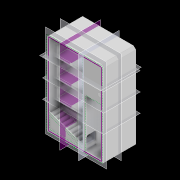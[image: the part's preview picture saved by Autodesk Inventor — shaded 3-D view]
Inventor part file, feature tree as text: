
AUTODESK INVENTOR PART (.ipt)
format: ipt  version: 2020 (Build 240168000, 168)  size: 2,139,136 bytes
history: native  units: mm
features: other x140, sketch x44, extrude x32, plane x15, mirror x15, pattern_linear x14, projected_geometry x8, chamfer x6, fillet x4, hole x2, loft x2
ambient origin geometry x8: Origin, YZ Plane, XZ Plane, XY Plane, X Axis, Y Axis, Z Axis, Center Point
bodies: Body1 (feature_tree), Body2 (feature_tree), Body3 (feature_tree), Body4 (feature_tree), Body5 (feature_tree), Body6 (feature_tree), Body7 (feature_tree), Body8 (feature_tree), Body9 (feature_tree), Body10 (feature_tree), Body11 (feature_tree), Body12 (feature_tree), Body13 (feature_tree), Body14 (feature_tree), Body15 (feature_tree), Body16 (feature_tree), Body17 (feature_tree), Body18 (feature_tree), Body19 (feature_tree), Body20 (feature_tree), Body21 (feature_tree), Body22 (feature_tree), Body23 (feature_tree), Body24 (feature_tree), Body25 (feature_tree), Body26 (feature_tree), Body27 (feature_tree), Body28 (feature_tree), Body29 (feature_tree), Body30 (feature_tree), Body31 (feature_tree), Body32 (feature_tree), Body33 (feature_tree), Body34 (feature_tree), Body35 (feature_tree), Body36 (feature_tree), Body37 (feature_tree), Body38 (feature_tree), Body39 (feature_tree), Body40 (feature_tree), Body41 (feature_tree), Body42 (feature_tree), Body43 (feature_tree), Body44 (feature_tree), Body45 (feature_tree), Body46 (feature_tree), Body47 (feature_tree), Body48 (feature_tree)
feature tree (282):
  other  "實體1"
  extrude  "擠出1"  Depth=1200.0mm
  plane  "工作平面1"
  plane  "工作平面2"
  other  "分割1"
  plane  "工作平面3"
  extrude  "擠出3"  Depth=800.0mm
  plane  "工作平面6"
  plane  "工作平面7"
  extrude  "擠出4"  Depth=1820.0mm TaperAngle=0.0deg
  hole  "孔1"  [1 undecoded]
  pattern_linear  "矩形陣列1"  Spacing1=-80.0mm  [1 undecoded]
  pattern_linear  "矩形陣列2"  Spacing1=-30.0mm  [1 undecoded]
  pattern_linear  "矩形陣列3"  Count1=3  [1 undecoded]
  plane  "工作平面8"
  mirror  "鏡射1"
  mirror  "鏡射2"
  mirror  "鏡射3"
  extrude  "擠出5"  Depth=30.0mm
  plane  "工作平面9"
  other  "迴轉1"
  extrude  "擠出6"  Depth=30.0mm
  other  "迴轉2"
  plane  "工作平面10"
  extrude  "擠出7"  Depth=30.0mm
  loft  "斷面混成1"
  pattern_linear  "矩形陣列4"  Spacing1=-1230.0mm  [1 undecoded]
  pattern_linear  "矩形陣列5"  Count1=40 Spacing1=-345.0mm
  mirror  "鏡射4"
  mirror  "鏡射5"
  mirror  "鏡射6"
  pattern_linear  "矩形陣列6"  Count1=10  [1 undecoded]
  pattern_linear  "矩形陣列7"  Count1=2 Spacing1=0.0mm
  mirror  "鏡射7"
  mirror  "鏡射8"
  mirror  "鏡射9"
  sketch  "草圖13"
  extrude  "擠出8"  Depth=20.0mm
  extrude  "擠出9"  Depth=20.0mm
  extrude  "擠出10"  Depth=50.0mm
  extrude  "擠出11"  Depth=50.0mm
  other  "迴轉3"
  other  "迴轉4"
  plane  "工作平面11"
  extrude  "擠出12"  Depth=50.0mm
  loft  "斷面混成2"
  extrude  "擠出13"  Depth=20.0mm
  hole  "孔2"  [1 undecoded]
  pattern_linear  "矩形陣列8"  Spacing1=15.0mm  [1 undecoded]
  pattern_linear  "矩形陣列9"  Spacing1=11.0mm  [1 undecoded]
  pattern_linear  "矩形陣列10"  Spacing1=11.0mm  [1 undecoded]
  pattern_linear  "矩形陣列11"  Spacing1=11.0mm  [1 undecoded]
  mirror  "鏡射10"
  mirror  "鏡射11"
  mirror  "鏡射12"
  pattern_linear  "矩形陣列12"  Spacing1=11.0mm  [1 undecoded]
  pattern_linear  "矩形陣列13"  Spacing1=11.0mm  [1 undecoded]
  mirror  "鏡射13"
  mirror  "鏡射14"
  mirror  "鏡射15"
  extrude  "擠出14"  Depth=11.0mm
  plane  "工作平面12"
  other  "直接編輯1"
  other  "直接編輯2"
  other  "直接編輯3"
  other  "直接編輯4"
  other  "直接編輯5"
  other  "直接編輯6"
  sketch  "草圖26"
  extrude  "擠出15"  Depth=5.0mm TaperAngle=0.0deg
  chamfer  "倒角1"  Distance=10.0mm
  extrude  "擠出16"  Depth=15.0mm
  extrude  "擠出17"  Depth=2.5mm
  extrude  "擠出18"  TaperAngle=90.0deg  [1 undecoded]
  extrude  "擠出19"  Depth=10.0mm
  pattern_linear  "矩形陣列14"  Spacing1=1142.5mm  [1 undecoded]
  extrude  "擠出20"  Depth=2.5mm
  sketch  "草圖33"
  extrude  "擠出21"  Depth=20.0mm
  extrude  "擠出22"  Depth=15.0mm
  extrude  "擠出23"  TaperAngle=90.0deg  [1 undecoded]
  extrude  "擠出24"  [1 undecoded]
  extrude  "擠出25"  Depth=25.0mm
  extrude  "擠出26"  Depth=5.0mm
  extrude  "擠出27"  Depth=10.0mm TaperAngle=0.0deg
  chamfer  "倒角2"  Angle=90.0deg  [1 undecoded]
  chamfer  "倒角3"  Angle=90.0deg  [1 undecoded]
  chamfer  "倒角4"  Distance=20.0mm
  chamfer  "倒角5"  Distance=20.0mm
  chamfer  "倒角6"  Distance=20.0mm
  fillet  "圓角1"  Radius=20.0mm
  extrude  "擠出28"  Depth=5.0mm
  sketch  "草圖43"
  extrude  "擠出29"  Depth=15.0mm
  fillet  "圓角2"  Radius=5.0mm
  plane  "工作平面13"
  other  "迴轉5"
  fillet  "圓角3"  Radius=10.0mm
  extrude  "擠出30"  Depth=200.0mm
  extrude  "擠出31"  Depth=200.0mm
  extrude  "擠出32"  Depth=15.0mm
  fillet  "圓角4"  Radius=15.0mm
  plane  "工作平面14"
  other  "迴轉6"
  plane  "工作平面15"
  extrude  "擠出33"  Depth=435.0mm TaperAngle=0.0deg
  sketch  "草圖1"
  sketch  "草圖3"
  plane  "工作平面4"
  plane  "工作平面5"
  sketch  "草圖5"
  other  "實體4"
  sketch  "草圖6"
  other  "陣列 實體4:1"
  other  "實體5"
  other  "陣列 實體4:2"
  other  "實體6"
  other  "陣列 實體4:3"
  other  "實體7"
  other  "陣列 實體5:4"
  other  "實體8"
  other  "陣列 實體6:5"
  other  "實體9"
  sketch  "草圖7"
  other  "實體10"
  sketch  "草圖8"
  sketch  "草圖9"
  sketch  "草圖10"
  other  "實體11"
  sketch  "草圖11"
  projected_geometry  "投影迴路1"
  sketch  "草圖12"
  projected_geometry  "投影迴路2"
  other  "陣列 實體10:6"
  other  "實體12"
  other  "陣列 實體10:7"
  other  "實體13"
  other  "陣列 實體10:8"
  other  "實體14"
  other  "陣列 實體12:9"
  other  "實體15"
  other  "陣列 實體13:10"
  other  "實體16"
  other  "陣列 實體11:11"
  other  "實體17"
  other  "陣列 實體11:12"
  other  "實體18"
  other  "陣列 實體11:13"
  other  "實體19"
  other  "陣列 實體17:14"
  other  "實體20"
  other  "陣列 實體18:15"
  other  "實體21"
  sketch  "草圖14"
  projected_geometry  "投影迴路3"
  other  "實體22"
  sketch  "草圖15"
  sketch  "草圖16"
  sketch  "草圖17"
  projected_geometry  "投影迴路4"
  projected_geometry  "投影迴路5"
  projected_geometry  "投影迴路6"
  other  "實體23"
  sketch  "草圖18"
  sketch  "草圖19"
  other  "實體24"
  sketch  "草圖20"
  projected_geometry  "投影迴路7"
  sketch  "草圖21"
  sketch  "草圖22"
  sketch  "草圖23"
  other  "陣列 實體22:16"
  other  "實體25"
  other  "陣列 實體22:17"
  other  "實體26"
  other  "陣列 實體23:18"
  other  "實體27"
  other  "陣列 實體23:19"
  other  "實體28"
  other  "陣列 實體23:20"
  other  "實體29"
  other  "陣列 實體27:21"
  other  "實體30"
  other  "陣列 實體28:22"
  other  "實體31"
  other  "陣列 實體24:23"
  other  "實體32"
  other  "陣列 實體24:24"
  other  "實體33"
  other  "陣列 實體24:25"
  other  "實體34"
  other  "陣列 實體32:26"
  other  "實體35"
  other  "陣列 實體33:27"
  other  "實體36"
  sketch  "草圖24"
  sketch  "草圖27"
  sketch  "草圖28"
  sketch  "草圖29"
  sketch  "草圖30"
  projected_geometry  "投影迴路8"
  sketch  "草圖31"
  other  "實體37"
  other  "陣列 實體37:28"
  other  "實體38"
  other  "陣列 實體37:29"
  other  "實體39"
  other  "陣列 實體37:30"
  other  "實體40"
  other  "陣列 實體37:31"
  other  "實體41"
  other  "陣列 實體37:32"
  other  "實體42"
  other  "陣列 實體37:33"
  other  "實體43"
  other  "陣列 實體37:34"
  other  "實體44"
  other  "陣列 實體37:35"
  other  "實體45"
  other  "陣列 實體37:36"
  other  "實體46"
  sketch  "草圖32"
  sketch  "草圖34"
  sketch  "草圖35"
  sketch  "草圖36"
  sketch  "草圖37"
  other  "實體47"
  sketch  "草圖38"
  other  "實體48"
  sketch  "草圖39"
  sketch  "草圖40"
  other  "實體49"
  sketch  "草圖42"
  sketch  "草圖44"
  sketch  "草圖45"
  sketch  "草圖46"
  sketch  "草圖47"
  sketch  "草圖48"
  other  "實體2"
  other  "實體3"
  other  "投影切割邊1"
  other  "投影切割邊2"
  other  "投影切割邊3"
  other  "投影切割邊4"
  other  "投影切割邊5"
  other  "投影切割邊6"
  other  "投影切割邊7"
  other  "投影切割邊8"
  other  "投影切割邊9"
  other  "投影切割邊10"
  other  "投影切割邊11"
  other  "投影切割邊12"
  other  "投影切割邊13"
  other  "投影切割邊14"
  other  "投影切割邊15"
  other  "投影切割邊16"
  other  "投影切割邊17"
  other  "移動1"
  other  "移動2"
  other  "移動3"
  other  "移動4"
  other  "移動5"
  other  "移動6"
  other  "投影切割邊18"
  other  "投影切割邊19"
  other  "投影切割邊20"
  other  "投影切割邊21"
  other  "投影切割邊22"
  other  "投影切割邊23"
  other  "投影切割邊24"
  other  "投影切割邊25"
  other  "投影切割邊26"
  other  "投影切割邊27"
  other  "投影切割邊28"
  other  "投影切割邊29"
  other  "投影切割邊31"
  other  "投影切割邊32"
  other  "投影切割邊33"
  other  "投影切割邊34"
  other  "投影切割邊35"
  other  "投影切割邊36"
  other  "投影切割邊37"
note: 19 required parameter values undecoded (feature->parameter linkage not recoverable at this tier; creation-order binding heuristic only, values carry confidence <= 0.55)
